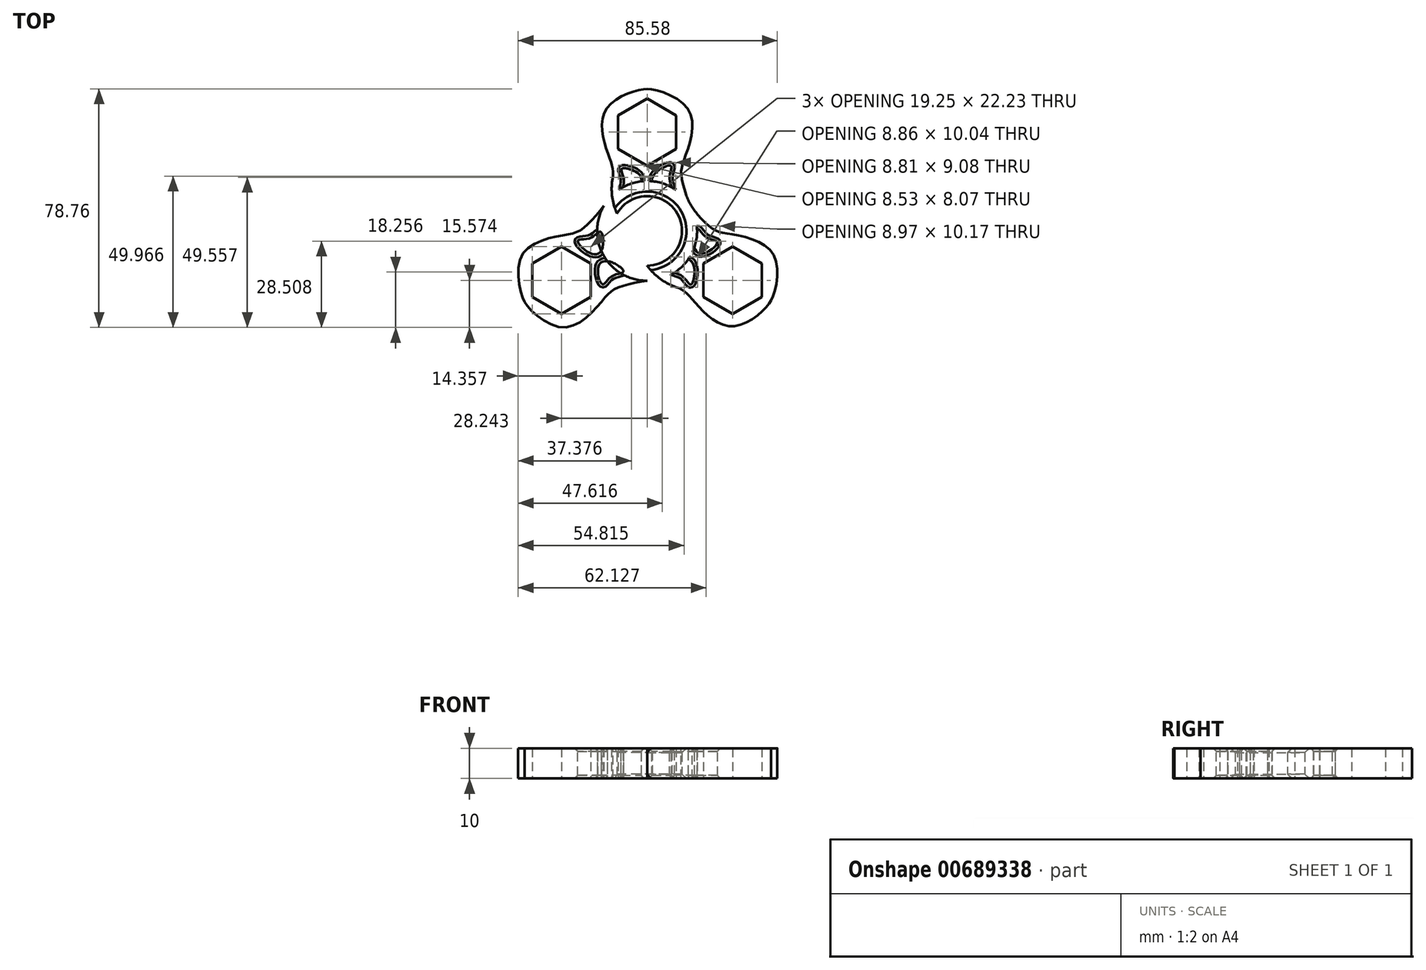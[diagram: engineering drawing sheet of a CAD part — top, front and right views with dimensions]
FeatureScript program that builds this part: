
annotation { "Feature Type Name" : "Feature", "Feature Type Description" : "" }
export const myFeature = defineFeature(function(context is Context, id is Id, definition is map)
    precondition{}
    {
        {
            var Q0;
            Q0=qCreatedBy(makeId("Top.planeOp"),FACE);
            var sketch = newSketch(context, id + "F0", { "sketchPlane" : qUnion([Q0])});
            skCircle(sketch, "E0", {"center": v(0, 0) * mm, "radius": 11.5 * mm});
            skLineSegment(sketch, "E1", {"start": v(0, 11.5) * mm, "end": v(-9.96, -5.75) * mm});
            skLineSegment(sketch, "E2", {"start": v(-9.96, -5.75) * mm, "end": v(9.96, -5.75) * mm});
            skLineSegment(sketch, "E3", {"start": v(9.96, -5.75) * mm, "end": v(0, 11.5) * mm});
            skCircle(sketch, "E4", {"center": v(0, 0) * mm, "radius": 16.5 * mm});
            skLineSegment(sketch, "E5", {"start": v(0, 11.5) * mm, "end": v(0, 21.5) * mm});
            skLineSegment(sketch, "E6", {"start": v(-9.96, -5.75) * mm, "end": v(4.98, 2.88) * mm});
            skLineSegment(sketch, "E7", {"start": v(0, -5.75) * mm, "end": v(0, 11.5) * mm});
            skLineSegment(sketch, "E8", {"start": v(-4.98, 2.88) * mm, "end": v(9.96, -5.75) * mm});
            skLineSegment(sketch, "E9", {"start": v(0, 0) * mm, "end": v(-18.62, -10.75) * mm});
            skLineSegment(sketch, "E10", {"start": v(0, 0) * mm, "end": v(18.62, -10.75) * mm});
            skLineSegment(sketch, "E11", {"start": v(-18.62, -10.75) * mm, "end": v(-9.96, -5.75) * mm});
            skLineSegment(sketch, "E12", {"start": v(9.96, -5.75) * mm, "end": v(18.62, -10.75) * mm});
            skLineSegment(sketch, "E13", {"start": v(-4.98, 2.88) * mm, "end": v(-14.29, 8.25) * mm});
            skLineSegment(sketch, "E14", {"start": v(4.98, 2.88) * mm, "end": v(14.29, 8.25) * mm});
            skLineSegment(sketch, "E15", {"start": v(0, -5.75) * mm, "end": v(0, -16.5) * mm});
            skCircle(sketch, "E16.cCircle", {"center": v(28.24, -16.3) * mm, "radius": 9.62 * mm, "construction": true});
            skLineSegment(sketch, "E16.0", {"start": v(28.24, -5.2) * mm, "end": v(37.87, -10.75) * mm});
            skLineSegment(sketch, "E16.1", {"start": v(37.87, -10.75) * mm, "end": v(37.87, -21.86) * mm});
            skLineSegment(sketch, "E16.2", {"start": v(37.87, -21.86) * mm, "end": v(28.24, -27.42) * mm});
            skLineSegment(sketch, "E16.3", {"start": v(28.24, -27.42) * mm, "end": v(18.62, -21.86) * mm});
            skLineSegment(sketch, "E16.4", {"start": v(18.62, -21.86) * mm, "end": v(18.62, -10.75) * mm});
            skLineSegment(sketch, "E16.5", {"start": v(18.62, -10.75) * mm, "end": v(28.24, -5.2) * mm});
            skPoint(sketch, "E16.0.midPoint", {"position": v(33.06, -7.97) * mm});
            skCircle(sketch, "E17.cCircle", {"center": v(0, 32.61) * mm, "radius": 9.62 * mm, "construction": true});
            skLineSegment(sketch, "E17.0", {"start": v(-9.62, 38.17) * mm, "end": v(0, 43.73) * mm});
            skLineSegment(sketch, "E17.1", {"start": v(0, 43.73) * mm, "end": v(9.62, 38.17) * mm});
            skLineSegment(sketch, "E17.2", {"start": v(9.62, 38.17) * mm, "end": v(9.62, 27.06) * mm});
            skLineSegment(sketch, "E17.3", {"start": v(9.62, 27.06) * mm, "end": v(0, 21.5) * mm});
            skLineSegment(sketch, "E17.4", {"start": v(0, 21.5) * mm, "end": v(-9.62, 27.06) * mm});
            skLineSegment(sketch, "E17.5", {"start": v(-9.62, 27.06) * mm, "end": v(-9.62, 38.17) * mm});
            skPoint(sketch, "E17.0.midPoint", {"position": v(-4.81, 40.95) * mm});
            skLineSegment(sketch, "E18", {"start": v(-18.62, -10.75) * mm, "end": v(-37.87, -21.86) * mm});
            skLineSegment(sketch, "E19", {"start": v(18.62, -10.75) * mm, "end": v(37.87, -21.86) * mm});
            skCircle(sketch, "E20.cCircle", {"center": v(-28.24, -16.3) * mm, "radius": 9.62 * mm, "construction": true});
            skLineSegment(sketch, "E20.0", {"start": v(-37.87, -10.75) * mm, "end": v(-28.24, -5.2) * mm});
            skLineSegment(sketch, "E20.1", {"start": v(-28.24, -5.2) * mm, "end": v(-18.62, -10.75) * mm});
            skLineSegment(sketch, "E20.2", {"start": v(-18.62, -10.75) * mm, "end": v(-18.62, -21.86) * mm});
            skLineSegment(sketch, "E20.3", {"start": v(-18.62, -21.86) * mm, "end": v(-28.24, -27.42) * mm});
            skLineSegment(sketch, "E20.4", {"start": v(-28.24, -27.42) * mm, "end": v(-37.87, -21.86) * mm});
            skLineSegment(sketch, "E20.5", {"start": v(-37.87, -21.86) * mm, "end": v(-37.87, -10.75) * mm});
            skPoint(sketch, "E20.0.midPoint", {"position": v(-33.06, -7.97) * mm});
            skFitSpline(sketch, "E21", {"points": [v(-14.29, 8.25) * mm, v(-11.3, 18.3) * mm, v(-12.42, 24.08) * mm, v(-13.7, 39.9) * mm, v(0, 46.88) * mm], "startDerivative": vector(17.83, 42.95) * mm, "endDerivative": vector(29.44, -0.34) * mm});
            skFitSpline(sketch, "E22.MirrorCS", {"points": [v(14.29, 8.25) * mm, v(11.3, 18.3) * mm, v(12.42, 24.08) * mm, v(13.7, 39.9) * mm, v(0, 46.88) * mm], "startDerivative": vector(-17.83, 42.95) * mm, "endDerivative": vector(-29.44, -0.34) * mm});
            skFitSpline(sketch, "E23", {"points": [v(0, -16.5) * mm, v(-10.19, -18.95) * mm, v(-14.63, -22.83) * mm, v(-27.68, -31.88) * mm, v(-40.42, -23.43) * mm], "startDerivative": vector(-46.1, -6.14) * mm, "endDerivative": vector(-12.55, 25.96) * mm});
            skFitSpline(sketch, "E24.MirrorCS", {"points": [v(-14.29, 8.25) * mm, v(-21.53, 0.59) * mm, v(-27.1, -1.35) * mm, v(-41.43, -8.19) * mm, v(-40.42, -23.43) * mm], "startDerivative": vector(-28.2, -36.98) * mm, "endDerivative": vector(14.03, -22.52) * mm});
            skFitSpline(sketch, "E25", {"points": [v(14.29, 8.25) * mm, v(21.44, 0.82) * mm, v(27.05, -1) * mm, v(41.5, -7.56) * mm, v(40.96, -22.92) * mm], "startDerivative": vector(28.92, -36.42) * mm, "endDerivative": vector(-16.87, -27.84) * mm});
            skFitSpline(sketch, "E26.MirrorCS", {"points": [v(0, -16.5) * mm, v(10.48, -18.94) * mm, v(15, -22.73) * mm, v(28.22, -31.52) * mm, v(40.96, -22.92) * mm], "startDerivative": vector(46.21, -5.23) * mm, "endDerivative": vector(13.08, 26.68) * mm});
            skFitSpline(sketch, "E27", {"points": [v(-8.4, 20.51) * mm, v(-7.67, 16.62) * mm, v(-8.25, 12.39) * mm, v(-3.06, 14.74) * mm, v(-2.62, 18.68) * mm, v(-8.4, 20.51) * mm]});
            skFitSpline(sketch, "E28", {"points": [v(8.08, 13.37) * mm, v(7.36, 17.26) * mm, v(7.94, 21.5) * mm, v(2.74, 19.14) * mm, v(2.31, 15.2) * mm, v(8.08, 13.37) * mm]});
            skFitSpline(sketch, "E29", {"points": [v(23.22, -3.83) * mm, v(19.62, -2.19) * mm, v(16.48, 0.71) * mm, v(15.44, -4.9) * mm, v(18.42, -7.51) * mm, v(23.22, -3.83) * mm]});
            skFitSpline(sketch, "E30", {"points": [v(7.78, -13.1) * mm, v(11.35, -14.79) * mm, v(14.45, -17.73) * mm, v(15.58, -12.14) * mm, v(12.64, -9.48) * mm, v(7.78, -13.1) * mm]});
            skFitSpline(sketch, "E31", {"points": [v(-14.74, -17.67) * mm, v(-11.77, -15.06) * mm, v(-7.84, -13.39) * mm, v(-12.52, -10.13) * mm, v(-16.12, -11.78) * mm, v(-14.74, -17.67) * mm]});
            skFitSpline(sketch, "E32", {"points": [v(-15.32, -0.31) * mm, v(-18.73, -2.32) * mm, v(-22.9, -3.23) * mm, v(-18.92, -7.3) * mm, v(-15.07, -6.36) * mm, v(-15.32, -0.31) * mm]});
            skSolve(sketch);
        }
        {
            var Q0;
            {var subQ1=sQuery(id+"F0.wireOp",EDGE,"E0");var subQ3=sQuery(id+"F0.wireOp",EDGE,"E15");var subQ4=makeQuery(id+"F0.imprint","INTERSECT",VERTEX,{"derivedFrom":[subQ1,subQ3]});Q0=makeQuery(id+"F0.imprint","IMPRINT",FACE,{"disambiguationData":[TD([[makeQuery(id+"F0.imprint","IMPRINT",EDGE,{"disambiguationData":[TD([[subQ4,-1.0]])],"derivedFrom":subQ1}),-1.0]])]});}
            var Q1;
            {var subQ0=sQuery(id+"F0.wireOp",EDGE,"E11");var subQ5=sQuery(id+"F0.wireOp",EDGE,"E4");var subQ7=makeQuery(id+"F0.imprint","INTERSECT",VERTEX,{"derivedFrom":[subQ5,subQ0]});Q1=makeQuery(id+"F0.imprint","IMPRINT",FACE,{"disambiguationData":[TD([[makeQuery(id+"F0.imprint","IMPRINT",EDGE,{"disambiguationData":[TD([[subQ7,-1.0]])],"derivedFrom":subQ5}),1.0]])]});}
            var Q2;
            {var subQ1=sQuery(id+"F0.wireOp",EDGE,"E0");var subQ3=sQuery(id+"F0.wireOp",EDGE,"E14");var subQ4=makeQuery(id+"F0.imprint","INTERSECT",VERTEX,{"derivedFrom":[subQ1,subQ3]});Q2=makeQuery(id+"F0.imprint","IMPRINT",FACE,{"disambiguationData":[TD([[makeQuery(id+"F0.imprint","IMPRINT",EDGE,{"disambiguationData":[TD([[subQ4,1.0]])],"derivedFrom":subQ1}),-1.0]])]});}
            var Q3;
            {var subQ0=sQuery(id+"F0.wireOp",EDGE,"E5");var subQ5=sQuery(id+"F0.wireOp",EDGE,"E4");var subQ7=makeQuery(id+"F0.imprint","INTERSECT",VERTEX,{"derivedFrom":[subQ5,subQ0]});Q3=makeQuery(id+"F0.imprint","IMPRINT",FACE,{"disambiguationData":[TD([[makeQuery(id+"F0.imprint","IMPRINT",EDGE,{"disambiguationData":[TD([[subQ7,1.0]])],"derivedFrom":subQ5}),1.0]])]});}
            var Q4;
            {var subQ0=sQuery(id+"F0.wireOp",EDGE,"E5");var subQ5=sQuery(id+"F0.wireOp",EDGE,"E4");var subQ7=makeQuery(id+"F0.imprint","INTERSECT",VERTEX,{"derivedFrom":[subQ5,subQ0]});Q4=makeQuery(id+"F0.imprint","IMPRINT",FACE,{"disambiguationData":[TD([[makeQuery(id+"F0.imprint","IMPRINT",EDGE,{"disambiguationData":[TD([[subQ7,-1.0]])],"derivedFrom":subQ5}),1.0]])]});}
            var Q5;
            {var subQ0=sQuery(id+"F0.wireOp",EDGE,"E11");var subQ5=sQuery(id+"F0.wireOp",EDGE,"E4");var subQ7=makeQuery(id+"F0.imprint","INTERSECT",VERTEX,{"derivedFrom":[subQ5,subQ0]});Q5=makeQuery(id+"F0.imprint","IMPRINT",FACE,{"disambiguationData":[TD([[makeQuery(id+"F0.imprint","IMPRINT",EDGE,{"disambiguationData":[TD([[subQ7,1.0]])],"derivedFrom":subQ5}),1.0]])]});}
            var Q6;
            Q6=makeQuery(id+"F0.imprint","IMPRINT",FACE,{"disambiguationData":[TD([[makeQuery(id+"F0.imprint","IMPRINT",EDGE,{"derivedFrom":sQuery(id+"F0.wireOp",EDGE,"E16.0")}),1.0]])]});
            var Q7;
            Q7=makeQuery(id+"F0.imprint","IMPRINT",FACE,{"disambiguationData":[TD([[makeQuery(id+"F0.imprint","IMPRINT",EDGE,{"derivedFrom":sQuery(id+"F0.wireOp",EDGE,"E17.0")}),1.0]])]});
            var Q8;
            Q8=makeQuery(id+"F0.imprint","IMPRINT",FACE,{"disambiguationData":[TD([[makeQuery(id+"F0.imprint","IMPRINT",EDGE,{"derivedFrom":sQuery(id+"F0.wireOp",EDGE,"E20.0")}),1.0]])]});
            extrude(context, id + "F1", {"entities" : qUnion([Q0, Q1, Q2, Q3, Q4, Q5, Q6, Q7, Q8]), "depth" : 10 * mm, "offsetDistance" : 25 * mm});
        }
        {
            var Q0;
            Q0=makeQuery(id+"F1.opExtrude","CAP_EDGE",EDGE,{"disambiguationData":[OSD([sQuery(id+"F0.wireOp",EDGE,"E0")])],"isStart":false});
            var Q1;
            Q1=makeQuery(id+"F1.opExtrude","CAP_EDGE",EDGE,{"disambiguationData":[OSD([sQuery(id+"F0.wireOp",EDGE,"E0")])],"isStart":true});
            chamfer(context, id + "F2", {"entities" : qUnion([Q0, Q1]), "width" : 1.5 * mm, "tangentPropagation" : true});
        }
        {
            var Q0;
            Q0=makeQuery(id+"F1.opExtrude","SWEPT_EDGE",EDGE,{"disambiguationData":[OSD([sQuery(id+"F0.wireOp",EDGE,"E4"),sQuery(id+"F0.wireOp",EDGE,"E13"),sQuery(id+"F0.wireOp",EDGE,"E21"),sQuery(id+"F0.wireOp",EDGE,"E24.MirrorCS")])]});
            var Q1;
            Q1=makeQuery(id+"F1.opExtrude","SWEPT_EDGE",EDGE,{"disambiguationData":[OSD([sQuery(id+"F0.wireOp",EDGE,"E4"),sQuery(id+"F0.wireOp",EDGE,"E14"),sQuery(id+"F0.wireOp",EDGE,"E22.MirrorCS"),sQuery(id+"F0.wireOp",EDGE,"E25")])]});
            var Q2;
            Q2=makeQuery(id+"F1.opExtrude","SWEPT_EDGE",EDGE,{"disambiguationData":[OSD([sQuery(id+"F0.wireOp",EDGE,"E4"),sQuery(id+"F0.wireOp",EDGE,"E15"),sQuery(id+"F0.wireOp",EDGE,"E23"),sQuery(id+"F0.wireOp",EDGE,"E26.MirrorCS")])]});
            fillet(context, id + "F3", {"entities" : qUnion([Q0, Q1, Q2]), "radius" : 20 * mm, "tangentPropagation" : true, "allowEdgeOverflow" : false});
        }
        {
            var Q0;
            Q0=makeQuery(id+"F1.opExtrude","CAP_EDGE",EDGE,{"disambiguationData":[OSD([sQuery(id+"F0.wireOp",EDGE,"E27")])],"isStart":true});
            var Q1;
            Q1=makeQuery(id+"F1.opExtrude","CAP_EDGE",EDGE,{"disambiguationData":[OSD([sQuery(id+"F0.wireOp",EDGE,"E27")])],"isStart":false});
            var Q2;
            Q2=makeQuery(id+"F1.opExtrude","CAP_EDGE",EDGE,{"disambiguationData":[OSD([sQuery(id+"F0.wireOp",EDGE,"E28")])],"isStart":true});
            var Q3;
            Q3=makeQuery(id+"F1.opExtrude","CAP_EDGE",EDGE,{"disambiguationData":[OSD([sQuery(id+"F0.wireOp",EDGE,"E28")])],"isStart":false});
            var Q4;
            Q4=makeQuery(id+"F1.opExtrude","CAP_EDGE",EDGE,{"disambiguationData":[OSD([sQuery(id+"F0.wireOp",EDGE,"E32")])],"isStart":true});
            var Q5;
            Q5=makeQuery(id+"F1.opExtrude","CAP_EDGE",EDGE,{"disambiguationData":[OSD([sQuery(id+"F0.wireOp",EDGE,"E32")])],"isStart":false});
            var Q6;
            Q6=makeQuery(id+"F1.opExtrude","CAP_EDGE",EDGE,{"disambiguationData":[OSD([sQuery(id+"F0.wireOp",EDGE,"E31")])],"isStart":true});
            var Q7;
            Q7=makeQuery(id+"F1.opExtrude","CAP_EDGE",EDGE,{"disambiguationData":[OSD([sQuery(id+"F0.wireOp",EDGE,"E31")])],"isStart":false});
            var Q8;
            Q8=makeQuery(id+"F1.opExtrude","CAP_EDGE",EDGE,{"disambiguationData":[OSD([sQuery(id+"F0.wireOp",EDGE,"E30")])],"isStart":true});
            var Q9;
            Q9=makeQuery(id+"F1.opExtrude","CAP_EDGE",EDGE,{"disambiguationData":[OSD([sQuery(id+"F0.wireOp",EDGE,"E30")])],"isStart":false});
            var Q10;
            Q10=makeQuery(id+"F1.opExtrude","CAP_EDGE",EDGE,{"disambiguationData":[OSD([sQuery(id+"F0.wireOp",EDGE,"E29")])],"isStart":true});
            var Q11;
            Q11=makeQuery(id+"F1.opExtrude","CAP_EDGE",EDGE,{"disambiguationData":[OSD([sQuery(id+"F0.wireOp",EDGE,"E29")])],"isStart":false});
            chamfer(context, id + "F4", {"entities" : qUnion([Q0, Q1, Q2, Q3, Q4, Q5, Q6, Q7, Q8, Q9, Q10, Q11]), "width" : 1 * mm, "tangentPropagation" : true});
        }
    });
